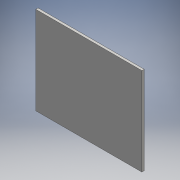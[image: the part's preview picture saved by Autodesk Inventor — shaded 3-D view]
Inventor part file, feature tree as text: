
AUTODESK INVENTOR PART (.ipt)
format: ipt  version: 2016 (Build 200138000, 138)  size: 88,064 bytes
history: native  units: mm
features: extrude x1, sketch x1
ambient origin geometry x8: Origin, YZ Plane, XZ Plane, XY Plane, X Axis, Y Axis, Z Axis, Center Point
bodies: Solid1 (feature_tree)
feature tree (2):
  extrude  "Extrusion1"  Depth=707.1mm
  sketch  "Sketch1"  dims[d0=853.55mm d1=707.1mm d2=19.0mm d3=0.0mm]
